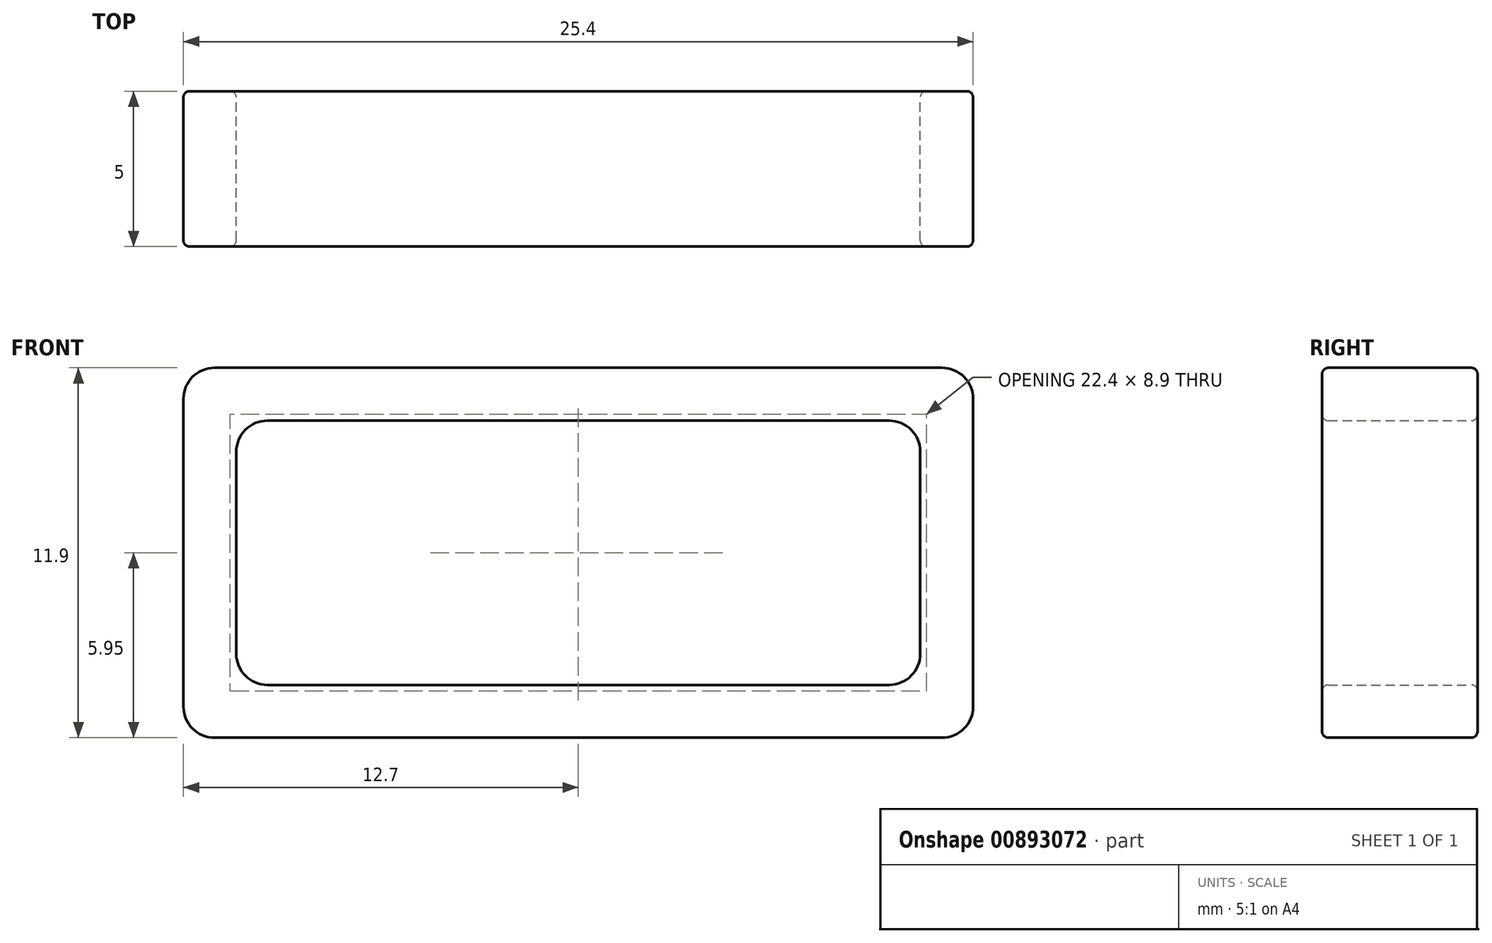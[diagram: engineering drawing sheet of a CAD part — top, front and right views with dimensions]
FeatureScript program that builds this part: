
annotation { "Feature Type Name" : "Feature", "Feature Type Description" : "" }
export const myFeature = defineFeature(function(context is Context, id is Id, definition is map)
    precondition{}
    {
        {
            var Q0;
            Q0=qCreatedBy(makeId("Front.planeOp"),FACE);
            var sketch = newSketch(context, id + "F0", { "sketchPlane" : qUnion([Q0])});
            skLineSegment(sketch, "E0.bottom", {"start": v(11, -4.25) * mm, "end": v(-11, -4.25) * mm});
            skLineSegment(sketch, "E0.top", {"start": v(11, 4.25) * mm, "end": v(-11, 4.25) * mm});
            skLineSegment(sketch, "E0.left", {"start": v(11, -4.25) * mm, "end": v(11, 4.25) * mm});
            skLineSegment(sketch, "E0.right", {"start": v(-11, -4.25) * mm, "end": v(-11, 4.25) * mm});
            skPoint(sketch, "E0.middle", {"position": v(0, 0) * mm});
            skLineSegment(sketch, "E1.bottom", {"start": v(12.7, -5.95) * mm, "end": v(-12.7, -5.95) * mm});
            skLineSegment(sketch, "E1.top", {"start": v(12.7, 5.95) * mm, "end": v(-12.7, 5.95) * mm});
            skLineSegment(sketch, "E1.left", {"start": v(12.7, -5.95) * mm, "end": v(12.7, 5.95) * mm});
            skLineSegment(sketch, "E1.right", {"start": v(-12.7, -5.95) * mm, "end": v(-12.7, 5.95) * mm});
            skSolve(sketch);
        }
        {
            var Q0;
            Q0 = qSketchRegion(id + "F0", true);
            extrude(context, id + "F1", {"entities" : qUnion([Q0]), "depth" : 5 * mm, "offsetDistance" : 25 * mm});
        }
        {
            var Q0;
            Q0=makeQuery(id+"F1.opExtrude","SWEPT_EDGE",EDGE,{"disambiguationData":[OSD([sQuery(id+"F0.wireOp",EDGE,"E1.top"),sQuery(id+"F0.wireOp",EDGE,"E1.right")])]});
            var Q1;
            Q1=makeQuery(id+"F1.opExtrude","SWEPT_EDGE",EDGE,{"disambiguationData":[OSD([sQuery(id+"F0.wireOp",EDGE,"E1.top"),sQuery(id+"F0.wireOp",EDGE,"E1.left")])]});
            var Q2;
            Q2=makeQuery(id+"F1.opExtrude","SWEPT_EDGE",EDGE,{"disambiguationData":[OSD([sQuery(id+"F0.wireOp",EDGE,"E1.bottom"),sQuery(id+"F0.wireOp",EDGE,"E1.left")])]});
            var Q3;
            Q3=makeQuery(id+"F1.opExtrude","SWEPT_EDGE",EDGE,{"disambiguationData":[OSD([sQuery(id+"F0.wireOp",EDGE,"E1.bottom"),sQuery(id+"F0.wireOp",EDGE,"E1.right")])]});
            var Q4;
            Q4=makeQuery(id+"F1.opExtrude","SWEPT_EDGE",EDGE,{"disambiguationData":[OSD([sQuery(id+"F0.wireOp",EDGE,"E0.top"),sQuery(id+"F0.wireOp",EDGE,"E0.right")])]});
            var Q5;
            Q5=makeQuery(id+"F1.opExtrude","SWEPT_EDGE",EDGE,{"disambiguationData":[OSD([sQuery(id+"F0.wireOp",EDGE,"E0.bottom"),sQuery(id+"F0.wireOp",EDGE,"E0.right")])]});
            var Q6;
            Q6=makeQuery(id+"F1.opExtrude","SWEPT_EDGE",EDGE,{"disambiguationData":[OSD([sQuery(id+"F0.wireOp",EDGE,"E0.top"),sQuery(id+"F0.wireOp",EDGE,"E0.left")])]});
            var Q7;
            Q7=makeQuery(id+"F1.opExtrude","SWEPT_EDGE",EDGE,{"disambiguationData":[OSD([sQuery(id+"F0.wireOp",EDGE,"E0.bottom"),sQuery(id+"F0.wireOp",EDGE,"E0.left")])]});
            fillet(context, id + "F2", {"entities" : qUnion([Q0, Q1, Q2, Q3, Q4, Q5, Q6, Q7]), "radius" : 1 * mm, "tangentPropagation" : true, "allowEdgeOverflow" : false});
        }
        {
            var Q0;
            Q0=makeQuery(id+"F1.opExtrude","CAP_EDGE",EDGE,{"disambiguationData":[OSD([sQuery(id+"F0.wireOp",EDGE,"E1.top")])],"isStart":true});
            var Q1;
            {var subQ0=sQuery(id+"F0.wireOp",EDGE,"E1.right");var subQ1=sQuery(id+"F0.wireOp",EDGE,"E1.top");Q1=makeQuery(id+"F2.opFillet","BLEND_EDGE",EDGE,{"blendedFrom":[makeQuery(id+"F1.opExtrude","SWEPT_EDGE",EDGE,{"disambiguationData":[OSD([subQ1,subQ0])]}),makeQuery(id+"F1.opExtrude","CAP_FACE",FACE,{"disambiguationData":[OSD([sQuery(id+"F0.wireOp",EDGE,"E0.bottom"),sQuery(id+"F0.wireOp",EDGE,"E0.top"),sQuery(id+"F0.wireOp",EDGE,"E0.left"),sQuery(id+"F0.wireOp",EDGE,"E0.right"),sQuery(id+"F0.wireOp",EDGE,"E1.bottom"),subQ1,sQuery(id+"F0.wireOp",EDGE,"E1.left"),subQ0])],"isStart":true})],"blendedInto":[makeQuery(id+"F1.opExtrude","CAP_FACE",FACE,{"disambiguationData":[OSD([sQuery(id+"F0.wireOp",EDGE,"E0.bottom"),sQuery(id+"F0.wireOp",EDGE,"E0.top"),sQuery(id+"F0.wireOp",EDGE,"E0.left"),sQuery(id+"F0.wireOp",EDGE,"E0.right"),sQuery(id+"F0.wireOp",EDGE,"E1.bottom"),subQ1,sQuery(id+"F0.wireOp",EDGE,"E1.left"),subQ0])],"isStart":true})]});}
            var Q2;
            Q2=makeQuery(id+"F1.opExtrude","CAP_EDGE",EDGE,{"disambiguationData":[OSD([sQuery(id+"F0.wireOp",EDGE,"E1.right")])],"isStart":true});
            var Q3;
            {var subQ0=sQuery(id+"F0.wireOp",EDGE,"E1.right");var subQ1=sQuery(id+"F0.wireOp",EDGE,"E1.bottom");Q3=makeQuery(id+"F2.opFillet","BLEND_EDGE",EDGE,{"blendedFrom":[makeQuery(id+"F1.opExtrude","SWEPT_EDGE",EDGE,{"disambiguationData":[OSD([subQ1,subQ0])]}),makeQuery(id+"F1.opExtrude","CAP_FACE",FACE,{"disambiguationData":[OSD([sQuery(id+"F0.wireOp",EDGE,"E0.bottom"),sQuery(id+"F0.wireOp",EDGE,"E0.top"),sQuery(id+"F0.wireOp",EDGE,"E0.left"),sQuery(id+"F0.wireOp",EDGE,"E0.right"),subQ1,sQuery(id+"F0.wireOp",EDGE,"E1.top"),sQuery(id+"F0.wireOp",EDGE,"E1.left"),subQ0])],"isStart":true})],"blendedInto":[makeQuery(id+"F1.opExtrude","CAP_FACE",FACE,{"disambiguationData":[OSD([sQuery(id+"F0.wireOp",EDGE,"E0.bottom"),sQuery(id+"F0.wireOp",EDGE,"E0.top"),sQuery(id+"F0.wireOp",EDGE,"E0.left"),sQuery(id+"F0.wireOp",EDGE,"E0.right"),subQ1,sQuery(id+"F0.wireOp",EDGE,"E1.top"),sQuery(id+"F0.wireOp",EDGE,"E1.left"),subQ0])],"isStart":true})]});}
            var Q4;
            Q4=makeQuery(id+"F1.opExtrude","CAP_EDGE",EDGE,{"disambiguationData":[OSD([sQuery(id+"F0.wireOp",EDGE,"E1.bottom")])],"isStart":true});
            var Q5;
            {var subQ0=sQuery(id+"F0.wireOp",EDGE,"E1.left");var subQ1=sQuery(id+"F0.wireOp",EDGE,"E1.bottom");Q5=makeQuery(id+"F2.opFillet","BLEND_EDGE",EDGE,{"blendedFrom":[makeQuery(id+"F1.opExtrude","SWEPT_EDGE",EDGE,{"disambiguationData":[OSD([subQ1,subQ0])]}),makeQuery(id+"F1.opExtrude","CAP_FACE",FACE,{"disambiguationData":[OSD([sQuery(id+"F0.wireOp",EDGE,"E0.bottom"),sQuery(id+"F0.wireOp",EDGE,"E0.top"),sQuery(id+"F0.wireOp",EDGE,"E0.left"),sQuery(id+"F0.wireOp",EDGE,"E0.right"),subQ1,sQuery(id+"F0.wireOp",EDGE,"E1.top"),subQ0,sQuery(id+"F0.wireOp",EDGE,"E1.right")])],"isStart":true})],"blendedInto":[makeQuery(id+"F1.opExtrude","CAP_FACE",FACE,{"disambiguationData":[OSD([sQuery(id+"F0.wireOp",EDGE,"E0.bottom"),sQuery(id+"F0.wireOp",EDGE,"E0.top"),sQuery(id+"F0.wireOp",EDGE,"E0.left"),sQuery(id+"F0.wireOp",EDGE,"E0.right"),subQ1,sQuery(id+"F0.wireOp",EDGE,"E1.top"),subQ0,sQuery(id+"F0.wireOp",EDGE,"E1.right")])],"isStart":true})]});}
            var Q6;
            Q6=makeQuery(id+"F1.opExtrude","CAP_EDGE",EDGE,{"disambiguationData":[OSD([sQuery(id+"F0.wireOp",EDGE,"E1.left")])],"isStart":true});
            var Q7;
            {var subQ0=sQuery(id+"F0.wireOp",EDGE,"E1.left");var subQ1=sQuery(id+"F0.wireOp",EDGE,"E1.top");Q7=makeQuery(id+"F2.opFillet","BLEND_EDGE",EDGE,{"blendedFrom":[makeQuery(id+"F1.opExtrude","SWEPT_EDGE",EDGE,{"disambiguationData":[OSD([subQ1,subQ0])]}),makeQuery(id+"F1.opExtrude","CAP_FACE",FACE,{"disambiguationData":[OSD([sQuery(id+"F0.wireOp",EDGE,"E0.bottom"),sQuery(id+"F0.wireOp",EDGE,"E0.top"),sQuery(id+"F0.wireOp",EDGE,"E0.left"),sQuery(id+"F0.wireOp",EDGE,"E0.right"),sQuery(id+"F0.wireOp",EDGE,"E1.bottom"),subQ1,subQ0,sQuery(id+"F0.wireOp",EDGE,"E1.right")])],"isStart":true})],"blendedInto":[makeQuery(id+"F1.opExtrude","CAP_FACE",FACE,{"disambiguationData":[OSD([sQuery(id+"F0.wireOp",EDGE,"E0.bottom"),sQuery(id+"F0.wireOp",EDGE,"E0.top"),sQuery(id+"F0.wireOp",EDGE,"E0.left"),sQuery(id+"F0.wireOp",EDGE,"E0.right"),sQuery(id+"F0.wireOp",EDGE,"E1.bottom"),subQ1,subQ0,sQuery(id+"F0.wireOp",EDGE,"E1.right")])],"isStart":true})]});}
            var Q8;
            Q8=makeQuery(id+"F1.opExtrude","CAP_EDGE",EDGE,{"disambiguationData":[OSD([sQuery(id+"F0.wireOp",EDGE,"E1.bottom")])],"isStart":false});
            var Q9;
            Q9=makeQuery(id+"F1.opExtrude","CAP_EDGE",EDGE,{"disambiguationData":[OSD([sQuery(id+"F0.wireOp",EDGE,"E1.left")])],"isStart":false});
            var Q10;
            {var subQ0=sQuery(id+"F0.wireOp",EDGE,"E1.left");var subQ1=sQuery(id+"F0.wireOp",EDGE,"E1.top");Q10=makeQuery(id+"F2.opFillet","BLEND_EDGE",EDGE,{"blendedFrom":[makeQuery(id+"F1.opExtrude","SWEPT_EDGE",EDGE,{"disambiguationData":[OSD([subQ1,subQ0])]}),makeQuery(id+"F1.opExtrude","CAP_FACE",FACE,{"disambiguationData":[OSD([sQuery(id+"F0.wireOp",EDGE,"E0.bottom"),sQuery(id+"F0.wireOp",EDGE,"E0.top"),sQuery(id+"F0.wireOp",EDGE,"E0.left"),sQuery(id+"F0.wireOp",EDGE,"E0.right"),sQuery(id+"F0.wireOp",EDGE,"E1.bottom"),subQ1,subQ0,sQuery(id+"F0.wireOp",EDGE,"E1.right")])],"isStart":false})],"blendedInto":[makeQuery(id+"F1.opExtrude","CAP_FACE",FACE,{"disambiguationData":[OSD([sQuery(id+"F0.wireOp",EDGE,"E0.bottom"),sQuery(id+"F0.wireOp",EDGE,"E0.top"),sQuery(id+"F0.wireOp",EDGE,"E0.left"),sQuery(id+"F0.wireOp",EDGE,"E0.right"),sQuery(id+"F0.wireOp",EDGE,"E1.bottom"),subQ1,subQ0,sQuery(id+"F0.wireOp",EDGE,"E1.right")])],"isStart":false})]});}
            var Q11;
            Q11=makeQuery(id+"F1.opExtrude","CAP_EDGE",EDGE,{"disambiguationData":[OSD([sQuery(id+"F0.wireOp",EDGE,"E1.top")])],"isStart":false});
            var Q12;
            {var subQ0=sQuery(id+"F0.wireOp",EDGE,"E1.right");var subQ1=sQuery(id+"F0.wireOp",EDGE,"E1.top");Q12=makeQuery(id+"F2.opFillet","BLEND_EDGE",EDGE,{"blendedFrom":[makeQuery(id+"F1.opExtrude","SWEPT_EDGE",EDGE,{"disambiguationData":[OSD([subQ1,subQ0])]}),makeQuery(id+"F1.opExtrude","CAP_FACE",FACE,{"disambiguationData":[OSD([sQuery(id+"F0.wireOp",EDGE,"E0.bottom"),sQuery(id+"F0.wireOp",EDGE,"E0.top"),sQuery(id+"F0.wireOp",EDGE,"E0.left"),sQuery(id+"F0.wireOp",EDGE,"E0.right"),sQuery(id+"F0.wireOp",EDGE,"E1.bottom"),subQ1,sQuery(id+"F0.wireOp",EDGE,"E1.left"),subQ0])],"isStart":false})],"blendedInto":[makeQuery(id+"F1.opExtrude","CAP_FACE",FACE,{"disambiguationData":[OSD([sQuery(id+"F0.wireOp",EDGE,"E0.bottom"),sQuery(id+"F0.wireOp",EDGE,"E0.top"),sQuery(id+"F0.wireOp",EDGE,"E0.left"),sQuery(id+"F0.wireOp",EDGE,"E0.right"),sQuery(id+"F0.wireOp",EDGE,"E1.bottom"),subQ1,sQuery(id+"F0.wireOp",EDGE,"E1.left"),subQ0])],"isStart":false})]});}
            var Q13;
            Q13=makeQuery(id+"F1.opExtrude","CAP_EDGE",EDGE,{"disambiguationData":[OSD([sQuery(id+"F0.wireOp",EDGE,"E1.right")])],"isStart":false});
            var Q14;
            {var subQ0=sQuery(id+"F0.wireOp",EDGE,"E1.left");var subQ1=sQuery(id+"F0.wireOp",EDGE,"E1.bottom");Q14=makeQuery(id+"F2.opFillet","BLEND_EDGE",EDGE,{"blendedFrom":[makeQuery(id+"F1.opExtrude","SWEPT_EDGE",EDGE,{"disambiguationData":[OSD([subQ1,subQ0])]}),makeQuery(id+"F1.opExtrude","CAP_FACE",FACE,{"disambiguationData":[OSD([sQuery(id+"F0.wireOp",EDGE,"E0.bottom"),sQuery(id+"F0.wireOp",EDGE,"E0.top"),sQuery(id+"F0.wireOp",EDGE,"E0.left"),sQuery(id+"F0.wireOp",EDGE,"E0.right"),subQ1,sQuery(id+"F0.wireOp",EDGE,"E1.top"),subQ0,sQuery(id+"F0.wireOp",EDGE,"E1.right")])],"isStart":false})],"blendedInto":[makeQuery(id+"F1.opExtrude","CAP_FACE",FACE,{"disambiguationData":[OSD([sQuery(id+"F0.wireOp",EDGE,"E0.bottom"),sQuery(id+"F0.wireOp",EDGE,"E0.top"),sQuery(id+"F0.wireOp",EDGE,"E0.left"),sQuery(id+"F0.wireOp",EDGE,"E0.right"),subQ1,sQuery(id+"F0.wireOp",EDGE,"E1.top"),subQ0,sQuery(id+"F0.wireOp",EDGE,"E1.right")])],"isStart":false})]});}
            var Q15;
            {var subQ0=sQuery(id+"F0.wireOp",EDGE,"E1.right");var subQ1=sQuery(id+"F0.wireOp",EDGE,"E1.bottom");Q15=makeQuery(id+"F2.opFillet","BLEND_EDGE",EDGE,{"blendedFrom":[makeQuery(id+"F1.opExtrude","SWEPT_EDGE",EDGE,{"disambiguationData":[OSD([subQ1,subQ0])]}),makeQuery(id+"F1.opExtrude","CAP_FACE",FACE,{"disambiguationData":[OSD([sQuery(id+"F0.wireOp",EDGE,"E0.bottom"),sQuery(id+"F0.wireOp",EDGE,"E0.top"),sQuery(id+"F0.wireOp",EDGE,"E0.left"),sQuery(id+"F0.wireOp",EDGE,"E0.right"),subQ1,sQuery(id+"F0.wireOp",EDGE,"E1.top"),sQuery(id+"F0.wireOp",EDGE,"E1.left"),subQ0])],"isStart":false})],"blendedInto":[makeQuery(id+"F1.opExtrude","CAP_FACE",FACE,{"disambiguationData":[OSD([sQuery(id+"F0.wireOp",EDGE,"E0.bottom"),sQuery(id+"F0.wireOp",EDGE,"E0.top"),sQuery(id+"F0.wireOp",EDGE,"E0.left"),sQuery(id+"F0.wireOp",EDGE,"E0.right"),subQ1,sQuery(id+"F0.wireOp",EDGE,"E1.top"),sQuery(id+"F0.wireOp",EDGE,"E1.left"),subQ0])],"isStart":false})]});}
            fillet(context, id + "F3", {"entities" : qUnion([Q0, Q1, Q2, Q3, Q4, Q5, Q6, Q7, Q8, Q9, Q10, Q11, Q12, Q13, Q14, Q15]), "radius" : 0.2 * mm, "tangentPropagation" : true, "allowEdgeOverflow" : false});
        }
        {
            var Q0;
            Q0=makeQuery(id+"F1.opExtrude","CAP_EDGE",EDGE,{"disambiguationData":[OSD([sQuery(id+"F0.wireOp",EDGE,"E0.bottom")])],"isStart":true});
            var Q1;
            {var subQ0=sQuery(id+"F0.wireOp",EDGE,"E0.left");var subQ1=sQuery(id+"F0.wireOp",EDGE,"E0.bottom");Q1=makeQuery(id+"F2.opFillet","BLEND_EDGE",EDGE,{"blendedFrom":[makeQuery(id+"F1.opExtrude","SWEPT_EDGE",EDGE,{"disambiguationData":[OSD([subQ1,subQ0])]}),makeQuery(id+"F1.opExtrude","CAP_FACE",FACE,{"disambiguationData":[OSD([subQ1,sQuery(id+"F0.wireOp",EDGE,"E0.top"),subQ0,sQuery(id+"F0.wireOp",EDGE,"E0.right"),sQuery(id+"F0.wireOp",EDGE,"E1.bottom"),sQuery(id+"F0.wireOp",EDGE,"E1.top"),sQuery(id+"F0.wireOp",EDGE,"E1.left"),sQuery(id+"F0.wireOp",EDGE,"E1.right")])],"isStart":true})],"blendedInto":[makeQuery(id+"F1.opExtrude","CAP_FACE",FACE,{"disambiguationData":[OSD([subQ1,sQuery(id+"F0.wireOp",EDGE,"E0.top"),subQ0,sQuery(id+"F0.wireOp",EDGE,"E0.right"),sQuery(id+"F0.wireOp",EDGE,"E1.bottom"),sQuery(id+"F0.wireOp",EDGE,"E1.top"),sQuery(id+"F0.wireOp",EDGE,"E1.left"),sQuery(id+"F0.wireOp",EDGE,"E1.right")])],"isStart":true})]});}
            var Q2;
            Q2=makeQuery(id+"F1.opExtrude","CAP_EDGE",EDGE,{"disambiguationData":[OSD([sQuery(id+"F0.wireOp",EDGE,"E0.left")])],"isStart":true});
            var Q3;
            {var subQ0=sQuery(id+"F0.wireOp",EDGE,"E0.left");var subQ1=sQuery(id+"F0.wireOp",EDGE,"E0.top");Q3=makeQuery(id+"F2.opFillet","BLEND_EDGE",EDGE,{"blendedFrom":[makeQuery(id+"F1.opExtrude","SWEPT_EDGE",EDGE,{"disambiguationData":[OSD([subQ1,subQ0])]}),makeQuery(id+"F1.opExtrude","CAP_FACE",FACE,{"disambiguationData":[OSD([sQuery(id+"F0.wireOp",EDGE,"E0.bottom"),subQ1,subQ0,sQuery(id+"F0.wireOp",EDGE,"E0.right"),sQuery(id+"F0.wireOp",EDGE,"E1.bottom"),sQuery(id+"F0.wireOp",EDGE,"E1.top"),sQuery(id+"F0.wireOp",EDGE,"E1.left"),sQuery(id+"F0.wireOp",EDGE,"E1.right")])],"isStart":true})],"blendedInto":[makeQuery(id+"F1.opExtrude","CAP_FACE",FACE,{"disambiguationData":[OSD([sQuery(id+"F0.wireOp",EDGE,"E0.bottom"),subQ1,subQ0,sQuery(id+"F0.wireOp",EDGE,"E0.right"),sQuery(id+"F0.wireOp",EDGE,"E1.bottom"),sQuery(id+"F0.wireOp",EDGE,"E1.top"),sQuery(id+"F0.wireOp",EDGE,"E1.left"),sQuery(id+"F0.wireOp",EDGE,"E1.right")])],"isStart":true})]});}
            var Q4;
            Q4=makeQuery(id+"F1.opExtrude","CAP_EDGE",EDGE,{"disambiguationData":[OSD([sQuery(id+"F0.wireOp",EDGE,"E0.top")])],"isStart":true});
            var Q5;
            Q5=makeQuery(id+"F1.opExtrude","CAP_EDGE",EDGE,{"disambiguationData":[OSD([sQuery(id+"F0.wireOp",EDGE,"E0.right")])],"isStart":true});
            var Q6;
            {var subQ0=sQuery(id+"F0.wireOp",EDGE,"E0.right");var subQ1=sQuery(id+"F0.wireOp",EDGE,"E0.bottom");Q6=makeQuery(id+"F2.opFillet","BLEND_EDGE",EDGE,{"blendedFrom":[makeQuery(id+"F1.opExtrude","SWEPT_EDGE",EDGE,{"disambiguationData":[OSD([subQ1,subQ0])]}),makeQuery(id+"F1.opExtrude","CAP_FACE",FACE,{"disambiguationData":[OSD([subQ1,sQuery(id+"F0.wireOp",EDGE,"E0.top"),sQuery(id+"F0.wireOp",EDGE,"E0.left"),subQ0,sQuery(id+"F0.wireOp",EDGE,"E1.bottom"),sQuery(id+"F0.wireOp",EDGE,"E1.top"),sQuery(id+"F0.wireOp",EDGE,"E1.left"),sQuery(id+"F0.wireOp",EDGE,"E1.right")])],"isStart":true})],"blendedInto":[makeQuery(id+"F1.opExtrude","CAP_FACE",FACE,{"disambiguationData":[OSD([subQ1,sQuery(id+"F0.wireOp",EDGE,"E0.top"),sQuery(id+"F0.wireOp",EDGE,"E0.left"),subQ0,sQuery(id+"F0.wireOp",EDGE,"E1.bottom"),sQuery(id+"F0.wireOp",EDGE,"E1.top"),sQuery(id+"F0.wireOp",EDGE,"E1.left"),sQuery(id+"F0.wireOp",EDGE,"E1.right")])],"isStart":true})]});}
            var Q7;
            {var subQ0=sQuery(id+"F0.wireOp",EDGE,"E0.right");var subQ1=sQuery(id+"F0.wireOp",EDGE,"E0.top");Q7=makeQuery(id+"F2.opFillet","BLEND_EDGE",EDGE,{"blendedFrom":[makeQuery(id+"F1.opExtrude","SWEPT_EDGE",EDGE,{"disambiguationData":[OSD([subQ1,subQ0])]}),makeQuery(id+"F1.opExtrude","CAP_FACE",FACE,{"disambiguationData":[OSD([sQuery(id+"F0.wireOp",EDGE,"E0.bottom"),subQ1,sQuery(id+"F0.wireOp",EDGE,"E0.left"),subQ0,sQuery(id+"F0.wireOp",EDGE,"E1.bottom"),sQuery(id+"F0.wireOp",EDGE,"E1.top"),sQuery(id+"F0.wireOp",EDGE,"E1.left"),sQuery(id+"F0.wireOp",EDGE,"E1.right")])],"isStart":true})],"blendedInto":[makeQuery(id+"F1.opExtrude","CAP_FACE",FACE,{"disambiguationData":[OSD([sQuery(id+"F0.wireOp",EDGE,"E0.bottom"),subQ1,sQuery(id+"F0.wireOp",EDGE,"E0.left"),subQ0,sQuery(id+"F0.wireOp",EDGE,"E1.bottom"),sQuery(id+"F0.wireOp",EDGE,"E1.top"),sQuery(id+"F0.wireOp",EDGE,"E1.left"),sQuery(id+"F0.wireOp",EDGE,"E1.right")])],"isStart":true})]});}
            var Q8;
            {var subQ0=sQuery(id+"F0.wireOp",EDGE,"E0.left");var subQ1=sQuery(id+"F0.wireOp",EDGE,"E0.top");Q8=makeQuery(id+"F2.opFillet","BLEND_EDGE",EDGE,{"blendedFrom":[makeQuery(id+"F1.opExtrude","SWEPT_EDGE",EDGE,{"disambiguationData":[OSD([subQ1,subQ0])]}),makeQuery(id+"F1.opExtrude","CAP_FACE",FACE,{"disambiguationData":[OSD([sQuery(id+"F0.wireOp",EDGE,"E0.bottom"),subQ1,subQ0,sQuery(id+"F0.wireOp",EDGE,"E0.right"),sQuery(id+"F0.wireOp",EDGE,"E1.bottom"),sQuery(id+"F0.wireOp",EDGE,"E1.top"),sQuery(id+"F0.wireOp",EDGE,"E1.left"),sQuery(id+"F0.wireOp",EDGE,"E1.right")])],"isStart":false})],"blendedInto":[makeQuery(id+"F1.opExtrude","CAP_FACE",FACE,{"disambiguationData":[OSD([sQuery(id+"F0.wireOp",EDGE,"E0.bottom"),subQ1,subQ0,sQuery(id+"F0.wireOp",EDGE,"E0.right"),sQuery(id+"F0.wireOp",EDGE,"E1.bottom"),sQuery(id+"F0.wireOp",EDGE,"E1.top"),sQuery(id+"F0.wireOp",EDGE,"E1.left"),sQuery(id+"F0.wireOp",EDGE,"E1.right")])],"isStart":false})]});}
            var Q9;
            {var subQ0=sQuery(id+"F0.wireOp",EDGE,"E0.left");var subQ1=sQuery(id+"F0.wireOp",EDGE,"E0.bottom");Q9=makeQuery(id+"F2.opFillet","BLEND_EDGE",EDGE,{"blendedFrom":[makeQuery(id+"F1.opExtrude","SWEPT_EDGE",EDGE,{"disambiguationData":[OSD([subQ1,subQ0])]}),makeQuery(id+"F1.opExtrude","CAP_FACE",FACE,{"disambiguationData":[OSD([subQ1,sQuery(id+"F0.wireOp",EDGE,"E0.top"),subQ0,sQuery(id+"F0.wireOp",EDGE,"E0.right"),sQuery(id+"F0.wireOp",EDGE,"E1.bottom"),sQuery(id+"F0.wireOp",EDGE,"E1.top"),sQuery(id+"F0.wireOp",EDGE,"E1.left"),sQuery(id+"F0.wireOp",EDGE,"E1.right")])],"isStart":false})],"blendedInto":[makeQuery(id+"F1.opExtrude","CAP_FACE",FACE,{"disambiguationData":[OSD([subQ1,sQuery(id+"F0.wireOp",EDGE,"E0.top"),subQ0,sQuery(id+"F0.wireOp",EDGE,"E0.right"),sQuery(id+"F0.wireOp",EDGE,"E1.bottom"),sQuery(id+"F0.wireOp",EDGE,"E1.top"),sQuery(id+"F0.wireOp",EDGE,"E1.left"),sQuery(id+"F0.wireOp",EDGE,"E1.right")])],"isStart":false})]});}
            var Q10;
            {var subQ0=sQuery(id+"F0.wireOp",EDGE,"E0.right");var subQ1=sQuery(id+"F0.wireOp",EDGE,"E0.bottom");Q10=makeQuery(id+"F2.opFillet","BLEND_EDGE",EDGE,{"blendedFrom":[makeQuery(id+"F1.opExtrude","SWEPT_EDGE",EDGE,{"disambiguationData":[OSD([subQ1,subQ0])]}),makeQuery(id+"F1.opExtrude","CAP_FACE",FACE,{"disambiguationData":[OSD([subQ1,sQuery(id+"F0.wireOp",EDGE,"E0.top"),sQuery(id+"F0.wireOp",EDGE,"E0.left"),subQ0,sQuery(id+"F0.wireOp",EDGE,"E1.bottom"),sQuery(id+"F0.wireOp",EDGE,"E1.top"),sQuery(id+"F0.wireOp",EDGE,"E1.left"),sQuery(id+"F0.wireOp",EDGE,"E1.right")])],"isStart":false})],"blendedInto":[makeQuery(id+"F1.opExtrude","CAP_FACE",FACE,{"disambiguationData":[OSD([subQ1,sQuery(id+"F0.wireOp",EDGE,"E0.top"),sQuery(id+"F0.wireOp",EDGE,"E0.left"),subQ0,sQuery(id+"F0.wireOp",EDGE,"E1.bottom"),sQuery(id+"F0.wireOp",EDGE,"E1.top"),sQuery(id+"F0.wireOp",EDGE,"E1.left"),sQuery(id+"F0.wireOp",EDGE,"E1.right")])],"isStart":false})]});}
            var Q11;
            Q11=makeQuery(id+"F1.opExtrude","CAP_EDGE",EDGE,{"disambiguationData":[OSD([sQuery(id+"F0.wireOp",EDGE,"E0.right")])],"isStart":false});
            var Q12;
            Q12=makeQuery(id+"F1.opExtrude","CAP_EDGE",EDGE,{"disambiguationData":[OSD([sQuery(id+"F0.wireOp",EDGE,"E0.top")])],"isStart":false});
            var Q13;
            Q13=makeQuery(id+"F1.opExtrude","CAP_EDGE",EDGE,{"disambiguationData":[OSD([sQuery(id+"F0.wireOp",EDGE,"E0.left")])],"isStart":false});
            var Q14;
            Q14=makeQuery(id+"F1.opExtrude","CAP_EDGE",EDGE,{"disambiguationData":[OSD([sQuery(id+"F0.wireOp",EDGE,"E0.bottom")])],"isStart":false});
            fillet(context, id + "F4", {"entities" : qUnion([Q0, Q1, Q2, Q3, Q4, Q5, Q6, Q7, Q8, Q9, Q10, Q11, Q12, Q13, Q14]), "radius" : .2 * mm, "tangentPropagation" : true, "allowEdgeOverflow" : false});
        }
    });
